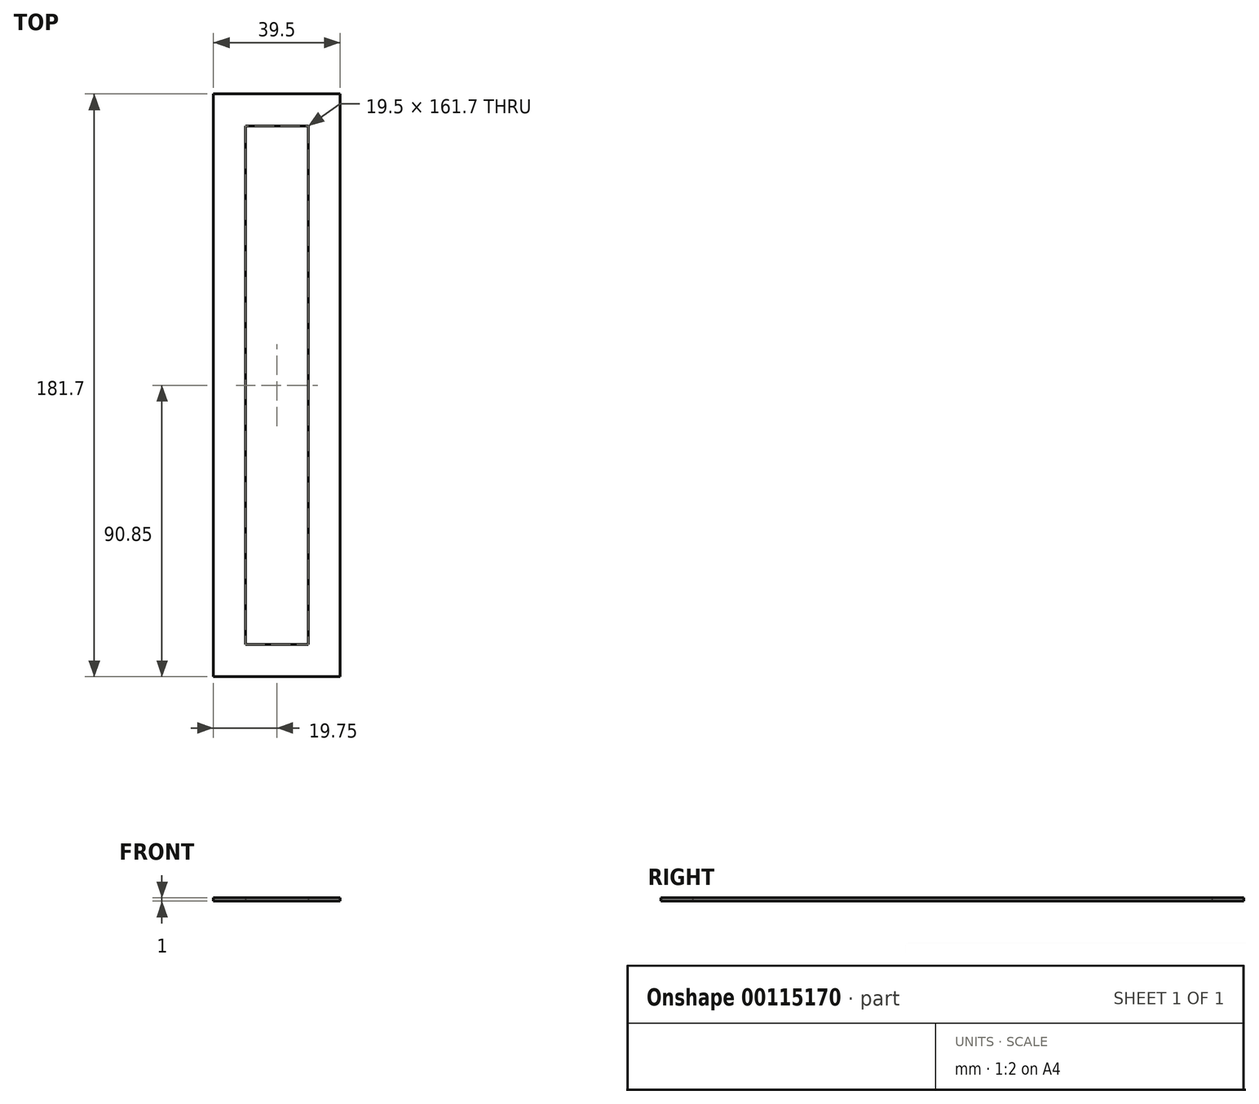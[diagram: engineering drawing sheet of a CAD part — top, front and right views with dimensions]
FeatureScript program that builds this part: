
annotation { "Feature Type Name" : "Feature", "Feature Type Description" : "" }
export const myFeature = defineFeature(function(context is Context, id is Id, definition is map)
    precondition{}
    {
        {
            var Q0;
            Q0=qCreatedBy(makeId("Top.planeOp"),FACE);
            var sketch = newSketch(context, id + "F0", { "sketchPlane" : qUnion([Q0])});
            skLineSegment(sketch, "E0.bottom", {"start": v(9.75, -80.85) * mm, "end": v(-9.75, -80.85) * mm});
            skLineSegment(sketch, "E0.top", {"start": v(9.75, 80.85) * mm, "end": v(-9.75, 80.85) * mm});
            skLineSegment(sketch, "E0.left", {"start": v(9.75, -80.85) * mm, "end": v(9.75, 80.85) * mm});
            skLineSegment(sketch, "E0.right", {"start": v(-9.75, -80.85) * mm, "end": v(-9.75, 80.85) * mm});
            skPoint(sketch, "E0.middle", {"position": v(0, 0) * mm});
            skLineSegment(sketch, "E1.0", {"start": v(19.75, 90.85) * mm, "end": v(-19.75, 90.85) * mm});
            skLineSegment(sketch, "E1.1", {"start": v(19.75, -90.85) * mm, "end": v(19.75, 90.85) * mm});
            skLineSegment(sketch, "E1.2", {"start": v(19.75, -90.85) * mm, "end": v(-19.75, -90.85) * mm});
            skLineSegment(sketch, "E1.3", {"start": v(-19.75, -90.85) * mm, "end": v(-19.75, 90.85) * mm});
            skSolve(sketch);
        }
        {
            var Q0;
            Q0=makeQuery(id+"F0.imprint","IMPRINT",FACE,{"disambiguationData":[TD([[makeQuery(id+"F0.imprint","IMPRINT",EDGE,{"derivedFrom":sQuery(id+"F0.wireOp",EDGE,"E0.bottom")}),1.0]])]});
            extrude(context, id + "F1", {"entities" : qUnion([Q0]), "depth" : 1 * mm});
        }
    });
